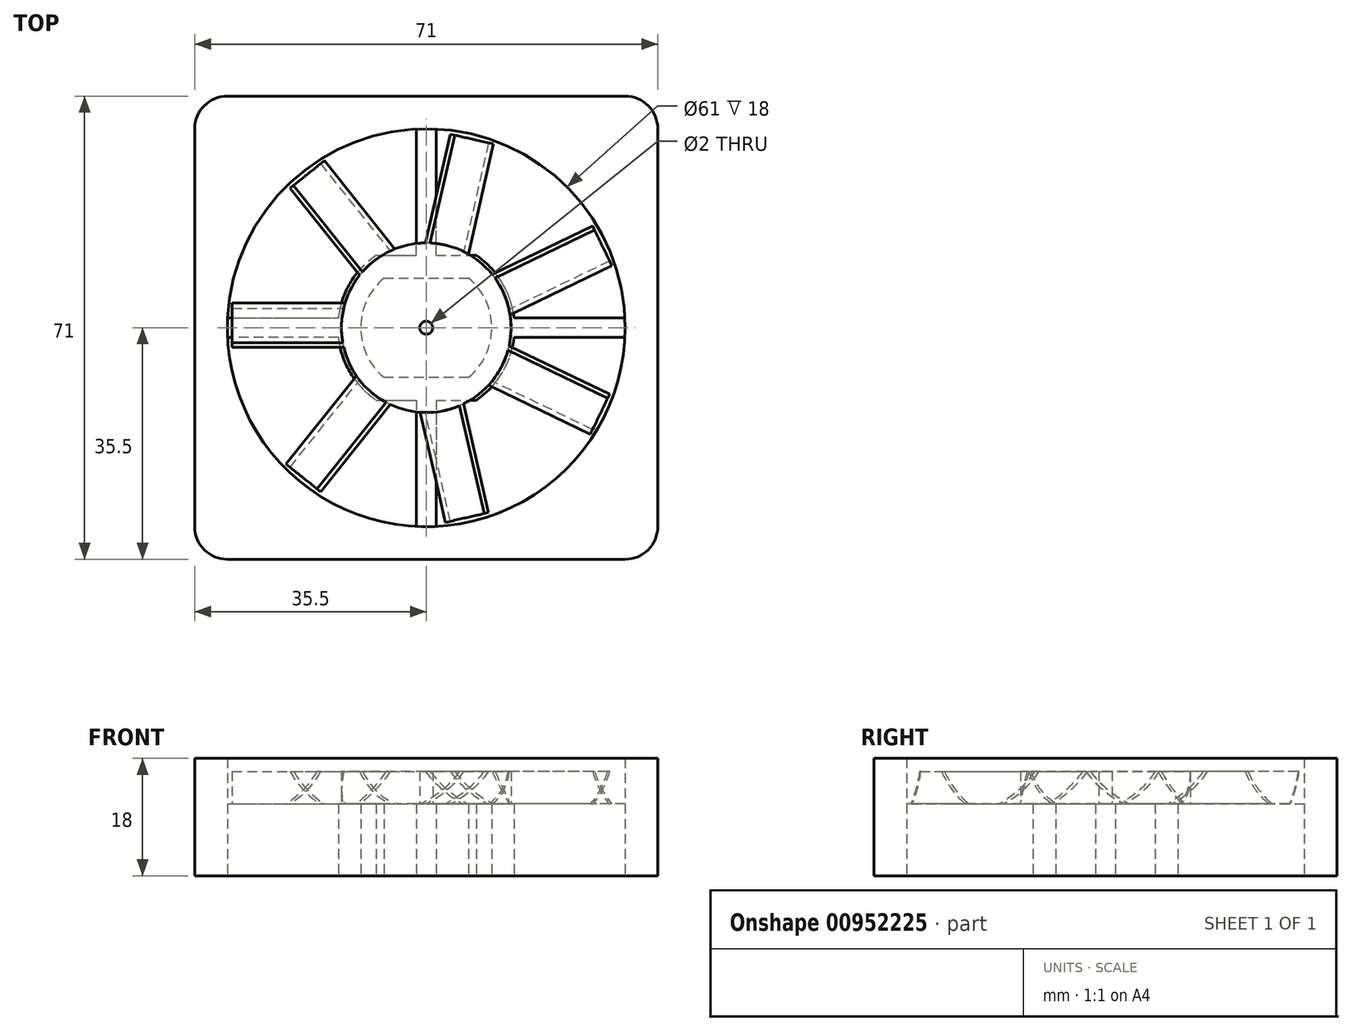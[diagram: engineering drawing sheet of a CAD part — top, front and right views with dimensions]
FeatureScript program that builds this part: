
annotation { "Feature Type Name" : "Feature", "Feature Type Description" : "" }
export const myFeature = defineFeature(function(context is Context, id is Id, definition is map)
    precondition{}
    {
        {
            var Q0;
            Q0=qCreatedBy(makeId("Top.planeOp"),FACE);
            var sketch = newSketch(context, id + "F0", { "sketchPlane" : qUnion([Q0])});
            skLineSegment(sketch, "E0", {"start": v(0, 0) * mm, "end": v(13, 0) * mm});
            skLineSegment(sketch, "E1", {"start": v(0, -15.2) * mm, "end": v(13, -15.2) * mm});
            skArc(sketch, "E2", {"start": v(13, -15.2) * mm, "mid": v(16.55, -7.6) * mm, "end": v(13, 0) * mm});
            skArc(sketch, "E3", {"start": v(0, 0) * mm, "mid": v(-3.55, -7.6) * mm, "end": v(0, -15.2) * mm});
            skLineSegment(sketch, "E4", {"start": v(6.5, 0) * mm, "end": v(6.5, -15.2) * mm});
            skPoint(sketch, "E5", {"position": v(6.5, -7.6) * mm});
            skCircle(sketch, "E6", {"center": v(6.5, -7.6) * mm, "radius": 30.5 * mm});
            skLineSegment(sketch, "E7.bottom", {"start": v(-29, 27.9) * mm, "end": v(42, 27.9) * mm});
            skLineSegment(sketch, "E7.top", {"start": v(-29, -43.1) * mm, "end": v(42, -43.1) * mm});
            skLineSegment(sketch, "E7.left", {"start": v(-29, 27.9) * mm, "end": v(-29, -43.1) * mm});
            skLineSegment(sketch, "E7.right", {"start": v(42, 27.9) * mm, "end": v(42, -43.1) * mm});
            skLineSegment(sketch, "E8", {"start": v(-29, 27.9) * mm, "end": v(42, -43.1) * mm, "construction": true});
            skLineSegment(sketch, "E9", {"start": v(42, 27.9) * mm, "end": v(-29, -43.1) * mm, "construction": true});
            skLineSegment(sketch, "E10.0", {"start": v(-1.16, 3.5) * mm, "end": v(14.16, 3.5) * mm});
            skArc(sketch, "E10.1", {"start": v(-1.16, 3.5) * mm, "mid": v(-7.05, -7.6) * mm, "end": v(-1.16, -18.7) * mm});
            skLineSegment(sketch, "E10.2", {"start": v(-1.16, -18.7) * mm, "end": v(14.16, -18.7) * mm});
            skArc(sketch, "E10.3", {"start": v(14.16, -18.7) * mm, "mid": v(20.05, -7.6) * mm, "end": v(14.16, 3.5) * mm});
            skLineSegment(sketch, "E11", {"start": v(6.5, 3.5) * mm, "end": v(6.5, 22.9) * mm, "construction": true});
            skLineSegment(sketch, "E12.0", {"start": v(8, 3.5) * mm, "end": v(8, 22.86) * mm});
            skLineSegment(sketch, "E13.0", {"start": v(5, 3.5) * mm, "end": v(5, 22.9) * mm});
            skLineSegment(sketch, "E14", {"start": v(6.5, -18.7) * mm, "end": v(6.5, -38.1) * mm, "construction": true});
            skLineSegment(sketch, "E15.0", {"start": v(5, -18.7) * mm, "end": v(5, -38.1) * mm});
            skLineSegment(sketch, "E16.0", {"start": v(8, -18.7) * mm, "end": v(8, -38.1) * mm});
            skLineSegment(sketch, "E17", {"start": v(20.05, -7.6) * mm, "end": v(37, -7.6) * mm, "construction": true});
            skLineSegment(sketch, "E18.0", {"start": v(20.05, -9.1) * mm, "end": v(37, -9.1) * mm});
            skLineSegment(sketch, "E19", {"start": v(20.05, -9.1) * mm, "end": v(19.97, -9.1) * mm});
            skLineSegment(sketch, "E20.0", {"start": v(20.05, -6.1) * mm, "end": v(37, -6.1) * mm});
            skLineSegment(sketch, "E21", {"start": v(20.05, -6.1) * mm, "end": v(19.97, -6.1) * mm});
            skLineSegment(sketch, "E22", {"start": v(-7.05, -7.6) * mm, "end": v(-24, -7.6) * mm, "construction": true});
            skLineSegment(sketch, "E23.0", {"start": v(-7.05, -6.1) * mm, "end": v(-24, -6.1) * mm});
            skLineSegment(sketch, "E24", {"start": v(-7.05, -6.1) * mm, "end": v(-6.97, -6.1) * mm});
            skLineSegment(sketch, "E25.0", {"start": v(-7.05, -9.1) * mm, "end": v(-24, -9.1) * mm});
            skLineSegment(sketch, "E26", {"start": v(-7.05, -9.1) * mm, "end": v(-6.97, -9.1) * mm});
            skSolve(sketch);
        }
        {
            var Q0;
            Q0=makeQuery(id+"F0.imprint","IMPRINT",FACE,{"disambiguationData":[TD([[makeQuery(id+"F0.imprint","IMPRINT",EDGE,{"derivedFrom":sQuery(id+"F0.wireOp",EDGE,"E6")}),-1.0]])]});
            var Q1;
            {var subQ0=sQuery(id+"F0.wireOp",EDGE,"E24");Q1=makeQuery(id+"F0.imprint","IMPRINT",FACE,{"disambiguationData":[TD([[makeQuery(id+"F0.imprint","IMPRINT",EDGE,{"derivedFrom":subQ0}),-1.0]])]});}
            var Q2;
            {var subQ11=sQuery(id+"F0.wireOp",EDGE,"E2");Q2=makeQuery(id+"F0.imprint","IMPRINT",FACE,{"disambiguationData":[TD([[makeQuery(id+"F0.imprint","IMPRINT",EDGE,{"derivedFrom":subQ11}),-1.0]])]});}
            var Q3;
            {var subQ0=sQuery(id+"F0.wireOp",EDGE,"E12.0");Q3=makeQuery(id+"F0.imprint","IMPRINT",FACE,{"disambiguationData":[TD([[makeQuery(id+"F0.imprint","IMPRINT",EDGE,{"derivedFrom":subQ0}),1.0]])]});}
            var Q4;
            {var subQ0=sQuery(id+"F0.wireOp",EDGE,"E19");Q4=makeQuery(id+"F0.imprint","IMPRINT",FACE,{"disambiguationData":[TD([[makeQuery(id+"F0.imprint","IMPRINT",EDGE,{"derivedFrom":subQ0}),-1.0]])]});}
            var Q5;
            {var subQ0=sQuery(id+"F0.wireOp",EDGE,"E15.0");var subQ1=sQuery(id+"F0.wireOp",EDGE,"E6");var subQ2=makeQuery(id+"F0.imprint","INTERSECT",VERTEX,{"derivedFrom":[subQ1,subQ0]});Q5=makeQuery(id+"F0.imprint","IMPRINT",FACE,{"disambiguationData":[TD([[makeQuery(id+"F0.imprint","IMPRINT",EDGE,{"disambiguationData":[TD([[subQ2,-1.0]])],"derivedFrom":subQ1}),1.0]])]});}
            extrude(context, id + "F1", {"entities" : qUnion([Q0, Q1, Q2, Q3, Q4, Q5]), "depth" : 11 * mm, "offsetDistance" : 25 * mm});
        }
        {
            var Q0;
            Q0=makeQuery(id+"F1.opExtrude","SWEPT_EDGE",EDGE,{"disambiguationData":[OSD([sQuery(id+"F0.wireOp",EDGE,"E7.bottom"),sQuery(id+"F0.wireOp",EDGE,"E7.left")])]});
            var Q1;
            Q1=makeQuery(id+"F1.opExtrude","SWEPT_EDGE",EDGE,{"disambiguationData":[OSD([sQuery(id+"F0.wireOp",EDGE,"E7.bottom"),sQuery(id+"F0.wireOp",EDGE,"E7.right")])]});
            var Q2;
            Q2=makeQuery(id+"F1.opExtrude","SWEPT_EDGE",EDGE,{"disambiguationData":[OSD([sQuery(id+"F0.wireOp",EDGE,"E7.top"),sQuery(id+"F0.wireOp",EDGE,"E7.right")])]});
            var Q3;
            Q3=makeQuery(id+"F1.opExtrude","SWEPT_EDGE",EDGE,{"disambiguationData":[OSD([sQuery(id+"F0.wireOp",EDGE,"E7.top"),sQuery(id+"F0.wireOp",EDGE,"E7.left")])]});
            fillet(context, id + "F2", {"entities" : qUnion([Q0, Q1, Q2, Q3]), "radius" : 5 * mm, "tangentPropagation" : true, "allowEdgeOverflow" : false});
        }
        {
            var Q0;
            Q0=makeQuery(id+"F1.opExtrude","CAP_FACE",FACE,{"disambiguationData":[OSD([sQuery(id+"F0.wireOp",EDGE,"E0"),sQuery(id+"F0.wireOp",EDGE,"E1"),sQuery(id+"F0.wireOp",EDGE,"E2"),sQuery(id+"F0.wireOp",EDGE,"E3"),sQuery(id+"F0.wireOp",EDGE,"E7.bottom"),sQuery(id+"F0.wireOp",EDGE,"E7.top"),sQuery(id+"F0.wireOp",EDGE,"E7.left"),sQuery(id+"F0.wireOp",EDGE,"E7.right")])],"isStart":false});
            var sketch = newSketch(context, id + "F3", { "sketchPlane" : qUnion([Q0])});
            skLineSegment(sketch, "E27.bottom", {"start": v(-29, 27.9) * mm, "end": v(42, 27.9) * mm});
            skLineSegment(sketch, "E27.top", {"start": v(-29, -43.1) * mm, "end": v(42, -43.1) * mm});
            skLineSegment(sketch, "E27.left", {"start": v(-29, 27.9) * mm, "end": v(-29, -43.1) * mm});
            skLineSegment(sketch, "E27.right", {"start": v(42, 27.9) * mm, "end": v(42, -43.1) * mm});
            skCircle(sketch, "E28", {"center": v(6.5, -7.6) * mm, "radius": 30.5 * mm});
            skSolve(sketch);
        }
        {
            var Q0;
            Q0=makeQuery(id+"F3.imprint","IMPRINT",FACE,{"disambiguationData":[TD([[makeQuery(id+"F3.imprint","IMPRINT",EDGE,{"derivedFrom":sQuery(id+"F3.wireOp",EDGE,"E28")}),-1.0]])]});
            extrude(context, id + "F4", {"entities" : qUnion([Q0]), "operationType" : NewBodyOperationType.ADD, "depth" : 7 * mm, "offsetDistance" : 25 * mm});
        }
        {
            var Q0;
            Q0=makeQuery(id+"F1.opExtrude","CAP_FACE",FACE,{"disambiguationData":[OSD([sQuery(id+"F0.wireOp",EDGE,"E0"),sQuery(id+"F0.wireOp",EDGE,"E1"),sQuery(id+"F0.wireOp",EDGE,"E2"),sQuery(id+"F0.wireOp",EDGE,"E3"),sQuery(id+"F0.wireOp",EDGE,"E7.bottom"),sQuery(id+"F0.wireOp",EDGE,"E7.top"),sQuery(id+"F0.wireOp",EDGE,"E7.left"),sQuery(id+"F0.wireOp",EDGE,"E7.right")])],"isStart":false});
            var sketch = newSketch(context, id + "F5", { "sketchPlane" : qUnion([Q0])});
            skCircle(sketch, "E29", {"center": v(6.5, -7.6) * mm, "radius": 13 * mm});
            skSolve(sketch);
        }
        {
            var Q0;
            Q0=makeQuery(id+"F5.imprint","IMPRINT",FACE,{"disambiguationData":[TD([[makeQuery(id+"F5.imprint","IMPRINT",EDGE,{"derivedFrom":sQuery(id+"F5.wireOp",EDGE,"E29")}),1.0]])]});
            var Q1;
            Q1=makeQuery(id+"F5.imprint","IMPRINT",FACE,{"disambiguationData":[TD([[makeQuery(id+"F5.imprint","IMPRINT",EDGE,{"derivedFrom":makeQuery(id+"F1.opExtrude","CAP_EDGE",EDGE,{"disambiguationData":[OSD([sQuery(id+"F0.wireOp",EDGE,"E0")])],"isStart":false})}),-1.0]])]});
            var Q2;
            {var subQ0=sQuery(id+"F5.wireOp",EDGE,"E29");var subQ1=sQuery(id+"F0.wireOp",EDGE,"E13.0");var subQ2=makeQuery(id+"F1.opExtrude","CAP_EDGE",EDGE,{"disambiguationData":[OSD([subQ1])],"isStart":false});var subQ3=makeQuery(id+"F5.imprint","INTERSECT",VERTEX,{"derivedFrom":[subQ2,subQ0]});Q2=makeQuery(id+"F5.imprint","IMPRINT",FACE,{"disambiguationData":[TD([[makeQuery(id+"F5.imprint","IMPRINT",EDGE,{"disambiguationData":[TD([[subQ3,-1.0]])],"derivedFrom":subQ0}),1.0]])]});}
            var Q3;
            {var subQ0=sQuery(id+"F5.wireOp",EDGE,"E29");var subQ1=sQuery(id+"F0.wireOp",EDGE,"E12.0");var subQ2=makeQuery(id+"F1.opExtrude","CAP_EDGE",EDGE,{"disambiguationData":[OSD([subQ1])],"isStart":false});var subQ3=makeQuery(id+"F5.imprint","INTERSECT",VERTEX,{"derivedFrom":[subQ2,subQ0]});Q3=makeQuery(id+"F5.imprint","IMPRINT",FACE,{"disambiguationData":[TD([[makeQuery(id+"F5.imprint","IMPRINT",EDGE,{"disambiguationData":[TD([[subQ3,1.0]])],"derivedFrom":subQ0}),1.0]])]});}
            var Q4;
            {var subQ0=sQuery(id+"F5.wireOp",EDGE,"E29");var subQ2=sQuery(id+"F0.wireOp",EDGE,"E15.0");var subQ5=makeQuery(id+"F1.opExtrude","CAP_EDGE",EDGE,{"disambiguationData":[OSD([subQ2])],"isStart":false});var subQ6=makeQuery(id+"F5.imprint","INTERSECT",VERTEX,{"derivedFrom":[subQ5,subQ0]});Q4=makeQuery(id+"F5.imprint","IMPRINT",FACE,{"disambiguationData":[TD([[makeQuery(id+"F5.imprint","IMPRINT",EDGE,{"disambiguationData":[TD([[subQ6,1.0]])],"derivedFrom":subQ0}),1.0]])]});}
            var Q5;
            {var subQ0=sQuery(id+"F5.wireOp",EDGE,"E29");var subQ1=sQuery(id+"F0.wireOp",EDGE,"E16.0");var subQ2=makeQuery(id+"F1.opExtrude","CAP_EDGE",EDGE,{"disambiguationData":[OSD([subQ1])],"isStart":false});var subQ3=makeQuery(id+"F5.imprint","INTERSECT",VERTEX,{"derivedFrom":[subQ2,subQ0]});Q5=makeQuery(id+"F5.imprint","IMPRINT",FACE,{"disambiguationData":[TD([[makeQuery(id+"F5.imprint","IMPRINT",EDGE,{"disambiguationData":[TD([[subQ3,-1.0]])],"derivedFrom":subQ0}),1.0]])]});}
            extrude(context, id + "F6", {"entities" : qUnion([Q0, Q1, Q2, Q3, Q4, Q5]), "depth" : 5 * mm, "offsetDistance" : 25 * mm});
        }
        {
            var Q0;
            Q0=qCreatedBy(makeId("Right.planeOp"),FACE);
            cPlane(context, id + "F7", {"entities" : qUnion([Q0]), "cplaneType" : CPlaneType.OFFSET, "offset" : 6.5 * mm, "width" : 150 * mm, "height" : 150 * mm});
        }
        {
            var Q0;
            Q0=qCreatedBy(id+"F7.planeOp",FACE);
            var sketch = newSketch(context, id + "F8", { "sketchPlane" : qUnion([Q0])});
            skLineSegment(sketch, "E30", {"start": v(-10.6, 11) * mm, "end": v(-4.6, 16) * mm, "construction": true});
            skLineSegment(sketch, "E31", {"start": v(-7.6, 11) * mm, "end": v(-7.6, 16) * mm});
            skLineSegment(sketch, "E32.0", {"start": v(-10.28, 10.62) * mm, "end": v(-5.8, 14.35) * mm, "construction": true});
            skLineSegment(sketch, "E33.0", {"start": v(-11.38, 11) * mm, "end": v(-5.15, 16.2) * mm, "construction": true});
            skLineSegment(sketch, "E34", {"start": v(-5.8, 14.35) * mm, "end": v(-5.57, 14.54) * mm});
            skArc(sketch, "E35", {"start": v(-11.38, 11) * mm, "mid": v(-7.95, 13.21) * mm, "end": v(-5.15, 16.2) * mm, "construction": true});
            skArc(sketch, "E36", {"start": v(-10.6, 11) * mm, "mid": v(-7.28, 13.12) * mm, "end": v(-4.6, 16) * mm, "construction": true});
            skLineSegment(sketch, "E37", {"start": v(-11.38, 11) * mm, "end": v(-10.6, 11) * mm, "construction": true});
            skLineSegment(sketch, "E38", {"start": v(-5.15, 16.2) * mm, "end": v(-4.6, 16) * mm, "construction": true});
            skArc(sketch, "E39", {"start": v(-11.38, 11) * mm, "mid": v(-7.95, 13.21) * mm, "end": v(-5.15, 16.2) * mm});
            skArc(sketch, "E40", {"start": v(-10.6, 11) * mm, "mid": v(-7.28, 13.12) * mm, "end": v(-4.6, 16) * mm});
            skLineSegment(sketch, "E41", {"start": v(-4.6, 16) * mm, "end": v(-5.33, 16) * mm, "construction": true});
            skLineSegment(sketch, "E42.MirrorCS", {"start": v(-10.6, 16) * mm, "end": v(-9.87, 16) * mm});
            skLineSegment(sketch, "E43.MirrorCS", {"start": v(-10.05, 16.2) * mm, "end": v(-10.6, 16) * mm});
            skLineSegment(sketch, "E44.MirrorCS", {"start": v(-9.4, 14.35) * mm, "end": v(-9.63, 14.54) * mm});
            skLineSegment(sketch, "E45.MirrorCS", {"start": v(-3.82, 11) * mm, "end": v(-4.6, 11) * mm});
            skArc(sketch, "E46.MirrorCS", {"start": v(-4.6, 11) * mm, "mid": v(-7.92, 13.12) * mm, "end": v(-10.6, 16) * mm});
            skArc(sketch, "E47.MirrorCS", {"start": v(-3.82, 11) * mm, "mid": v(-7.25, 13.21) * mm, "end": v(-10.05, 16.2) * mm});
            skLineSegment(sketch, "E48.MirrorCS", {"start": v(-3.82, 11) * mm, "end": v(-10.05, 16.2) * mm, "construction": true});
            skLineSegment(sketch, "E49.MirrorCS", {"start": v(-4.6, 11) * mm, "end": v(-10.6, 16) * mm, "construction": true});
            skLineSegment(sketch, "E50.MirrorCS", {"start": v(-4.92, 10.62) * mm, "end": v(-9.4, 14.35) * mm, "construction": true});
            skSolve(sketch);
        }
        {
            var Q0;
            {var subQ0=sQuery(id+"F8.wireOp",EDGE,"E47.MirrorCS");var subQ3=sQuery(id+"F8.wireOp",EDGE,"E40");var subQ5=makeQuery(id+"F8.imprint","INTERSECT",VERTEX,{"derivedFrom":[subQ3,subQ0]});Q0=makeQuery(id+"F8.imprint","IMPRINT",FACE,{"disambiguationData":[TD([[makeQuery(id+"F8.imprint","IMPRINT",EDGE,{"disambiguationData":[TD([[subQ5,1.0]])],"derivedFrom":subQ3}),1.0]])]});}
            var Q1;
            {var subQ0=sQuery(id+"F8.wireOp",EDGE,"E39");var subQ3=sQuery(id+"F8.wireOp",EDGE,"E46.MirrorCS");var subQ5=makeQuery(id+"F8.imprint","INTERSECT",VERTEX,{"derivedFrom":[subQ0,subQ3]});Q1=makeQuery(id+"F8.imprint","IMPRINT",FACE,{"disambiguationData":[TD([[makeQuery(id+"F8.imprint","IMPRINT",EDGE,{"disambiguationData":[TD([[subQ5,-1.0]])],"derivedFrom":subQ0}),-1.0]])]});}
            var Q2;
            {var subQ0=sQuery(id+"F8.wireOp",EDGE,"E46.MirrorCS");var subQ1=sQuery(id+"F8.wireOp",EDGE,"E39");var subQ2=makeQuery(id+"F8.imprint","INTERSECT",VERTEX,{"derivedFrom":[subQ1,subQ0]});Q2=makeQuery(id+"F8.imprint","IMPRINT",FACE,{"disambiguationData":[TD([[makeQuery(id+"F8.imprint","IMPRINT",EDGE,{"disambiguationData":[TD([[subQ2,-1.0]])],"derivedFrom":subQ1}),1.0]])]});}
            var Q3;
            {var subQ5=sQuery(id+"F8.wireOp",EDGE,"E45.MirrorCS");Q3=makeQuery(id+"F8.imprint","IMPRINT",FACE,{"disambiguationData":[TD([[makeQuery(id+"F8.imprint","IMPRINT",EDGE,{"derivedFrom":subQ5}),-1.0]])]});}
            extrude(context, id + "F9", {"entities" : qUnion([Q0, Q1, Q2, Q3]), "oppositeDirection" : true, "depth" : 29.75 * mm, "offsetDistance" : 25 * mm});
        }
        {
            var Q0;
            Q0=makeQuery(id+"F9.opExtrude","SWEPT_BODY",BODY,{"disambiguationData":[OSD([sQuery(id+"F8.wireOp",EDGE,"E42.MirrorCS"),sQuery(id+"F8.wireOp",EDGE,"E45.MirrorCS"),sQuery(id+"F8.wireOp",EDGE,"E46.MirrorCS"),sQuery(id+"F8.wireOp",EDGE,"E47.MirrorCS")])]});
            var Q1;
            Q1=sQuery(id+"F8.wireOp",EDGE,"E31");
            circularPattern(context, id + "F10", {"operationType" : NewBodyOperationType.ADD, "entities" : qUnion([Q0]), "axis" : qUnion([Q1]), "angle" : 360 * degree, "instanceCount" : 7, "equalSpace" : true});
        }
        {
            var Q0;
            Q0=makeQuery(id+"F5.imprint","IMPRINT",FACE,{"disambiguationData":[TD([[makeQuery(id+"F5.imprint","IMPRINT",EDGE,{"derivedFrom":makeQuery(id+"F1.opExtrude","CAP_EDGE",EDGE,{"disambiguationData":[OSD([sQuery(id+"F0.wireOp",EDGE,"E0")])],"isStart":false})}),-1.0]])]});
            var sketch = newSketch(context, id + "F11", { "sketchPlane" : qUnion([Q0])});
            skCircle(sketch, "E51", {"center": v(6.5, -7.6) * mm, "radius": 1 * mm});
            skSolve(sketch);
        }
        {
            var Q0;
            {var subQ0=sQuery(id+"F11.wireOp",EDGE,"E51");var subQ1=makeQuery(id+"F0.imprint","IMPRINT",EDGE,{"derivedFrom":sQuery(id+"F0.wireOp",EDGE,"E4")});var subQ2=makeQuery(id+"F11.imprint","INTERSECT",VERTEX,{"disambiguationData":[OD(0.0)],"derivedFrom":[subQ1,subQ0]});Q0=makeQuery(id+"F11.imprint","IMPRINT",FACE,{"disambiguationData":[TD([[makeQuery(id+"F11.imprint","IMPRINT",EDGE,{"disambiguationData":[TD([[subQ2,-1.0]])],"derivedFrom":subQ0}),1.0]])]});}
            var Q1;
            {var subQ0=sQuery(id+"F11.wireOp",EDGE,"E51");var subQ1=makeQuery(id+"F0.imprint","IMPRINT",EDGE,{"derivedFrom":sQuery(id+"F0.wireOp",EDGE,"E4")});var subQ2=makeQuery(id+"F11.imprint","INTERSECT",VERTEX,{"disambiguationData":[OD(0.0)],"derivedFrom":[subQ1,subQ0]});Q1=makeQuery(id+"F11.imprint","IMPRINT",FACE,{"disambiguationData":[TD([[makeQuery(id+"F11.imprint","IMPRINT",EDGE,{"disambiguationData":[TD([[subQ2,1.0]])],"derivedFrom":subQ0}),1.0]])]});}
            extrude(context, id + "F12", {"entities" : qUnion([Q0, Q1]), "operationType" : NewBodyOperationType.REMOVE, "depth" : 7.2 * mm, "offsetDistance" : 25 * mm});
        }
    });
